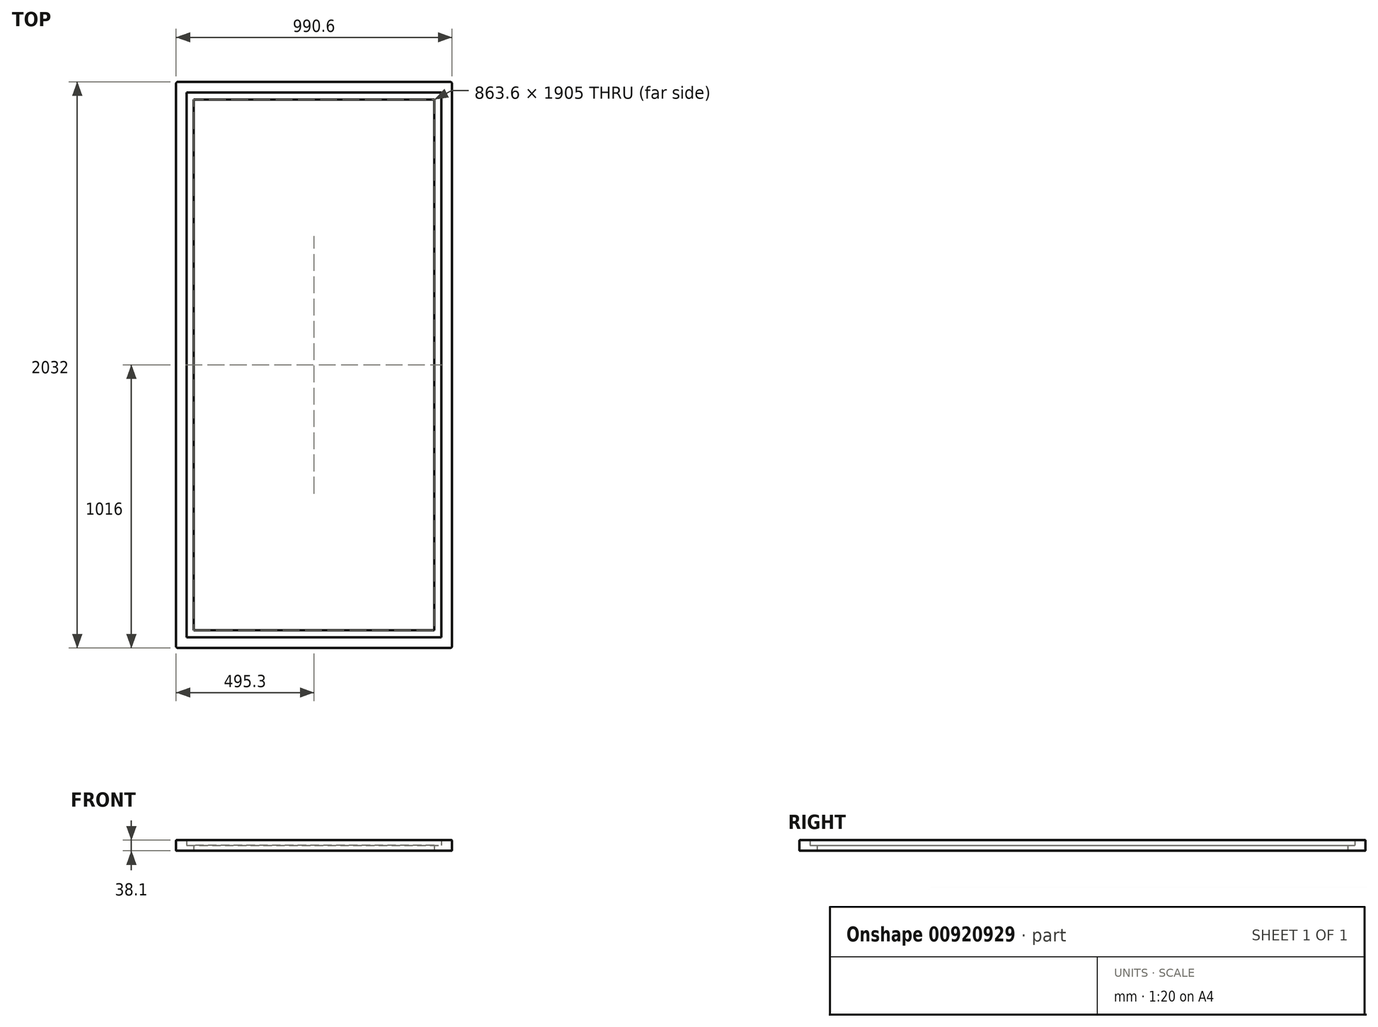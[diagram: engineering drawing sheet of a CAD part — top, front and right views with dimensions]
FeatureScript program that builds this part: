
annotation { "Feature Type Name" : "Feature", "Feature Type Description" : "" }
export const myFeature = defineFeature(function(context is Context, id is Id, definition is map)
    precondition{}
    {
        {
            assignVariable(context, id + "F0", {"name" : "mbrdThick", "anyValue" : 19.05 * mm});
        }
        {
            var Q0;
            Q0=qCreatedBy(makeId("Top.planeOp"),FACE);
            var sketch = newSketch(context, id + "F1", { "sketchPlane" : qUnion([Q0])});
            skLineSegment(sketch, "E0.bottom", {"start": v(-495.3, 1016) * mm, "end": v(495.3, 1016) * mm, "construction": true});
            skLineSegment(sketch, "E0.left", {"start": v(-495.3, 1016) * mm, "end": v(-495.3, -1016) * mm, "construction": true});
            skLineSegment(sketch, "E0.right", {"start": v(495.3, 1016) * mm, "end": v(495.3, -1016) * mm, "construction": true});
            skPoint(sketch, "E0.middle", {"position": v(0, 0) * mm});
            skLineSegment(sketch, "E1.bottom", {"start": v(-495.3, 1016) * mm, "end": v(-431.8, 1016) * mm});
            skLineSegment(sketch, "E1.left", {"start": v(-495.3, 1016) * mm, "end": v(-495.3, -1016) * mm});
            skPoint(sketch, "E2", {"position": v(-431.8, 952.5) * mm});
            skLineSegment(sketch, "E3", {"start": v(-431.8, 952.5) * mm, "end": v(-495.3, 1016) * mm});
            skPoint(sketch, "E4", {"position": v(-431.8, -952.5) * mm});
            skLineSegment(sketch, "E5", {"start": v(-495.3, -1016) * mm, "end": v(-431.8, -952.5) * mm});
            skLineSegment(sketch, "E6", {"start": v(-431.8, 952.5) * mm, "end": v(-431.8, -952.5) * mm});
            skPoint(sketch, "E7", {"position": v(431.8, -952.5) * mm});
            skLineSegment(sketch, "E8", {"start": v(495.3, -1016) * mm, "end": v(431.8, -952.5) * mm});
            skLineSegment(sketch, "E9", {"start": v(431.8, -952.5) * mm, "end": v(-431.8, -952.5) * mm});
            skLineSegment(sketch, "E10", {"start": v(-495.3, -1016) * mm, "end": v(495.3, -1016) * mm});
            skLineSegment(sketch, "E11.1.0", {"start": v(431.8, -952.5) * mm, "end": v(431.8, 952.5) * mm});
            skLineSegment(sketch, "E11.1.1", {"start": v(495.3, -1016) * mm, "end": v(-495.3, -1016) * mm, "construction": true});
            skLineSegment(sketch, "E11.1.3", {"start": v(495.3, -1016) * mm, "end": v(495.3, 1016) * mm, "construction": true});
            skLineSegment(sketch, "E11.1.4", {"start": v(-495.3, -1016) * mm, "end": v(-495.3, 1016) * mm, "construction": true});
            skPoint(sketch, "E11.1.5", {"position": v(431.8, 952.5) * mm});
            skLineSegment(sketch, "E11.1.8", {"start": v(-431.8, 952.5) * mm, "end": v(431.8, 952.5) * mm});
            skLineSegment(sketch, "E11.1.9", {"start": v(495.3, 1016) * mm, "end": v(-495.3, 1016) * mm});
            skLineSegment(sketch, "E11.1.10", {"start": v(495.3, -1016) * mm, "end": v(495.3, 1016) * mm});
            skLineSegment(sketch, "E11.1.11", {"start": v(431.8, -952.5) * mm, "end": v(495.3, -1016) * mm});
            skLineSegment(sketch, "E11.1.12", {"start": v(-495.3, 1016) * mm, "end": v(-431.8, 952.5) * mm});
            skLineSegment(sketch, "E11.1.13", {"start": v(495.3, -1016) * mm, "end": v(431.8, -1016) * mm});
            skLineSegment(sketch, "E11.1.14", {"start": v(495.3, 1016) * mm, "end": v(431.8, 952.5) * mm});
            skLineSegment(sketch, "E11.anchor1", {"start": v(0, 0) * mm, "end": v(-495.3, -1016) * mm, "construction": true});
            skLineSegment(sketch, "E11.anchor2", {"start": v(0, 0) * mm, "end": v(495.3, 1016) * mm, "construction": true});
            skSolve(sketch);
        }
        {
            var Q0;
            Q0=makeQuery(id+"F1.imprint","IMPRINT",FACE,{"disambiguationData":[TD([[makeQuery(id+"F1.imprint","IMPRINT",EDGE,{"derivedFrom":sQuery(id+"F1.wireOp",EDGE,"E11.1.0")}),-1.0]])]});
            var Q1;
            Q1=makeQuery(id+"F1.imprint","IMPRINT",FACE,{"disambiguationData":[TD([[makeQuery(id+"F1.imprint","IMPRINT",EDGE,{"derivedFrom":sQuery(id+"F1.wireOp",EDGE,"E11.1.8")}),1.0]])]});
            var Q2;
            Q2=makeQuery(id+"F1.imprint","IMPRINT",FACE,{"disambiguationData":[TD([[makeQuery(id+"F1.imprint","IMPRINT",EDGE,{"derivedFrom":sQuery(id+"F1.wireOp",EDGE,"E1.left")}),1.0]])]});
            var Q3;
            Q3=makeQuery(id+"F1.imprint","IMPRINT",FACE,{"disambiguationData":[TD([[makeQuery(id+"F1.imprint","IMPRINT",EDGE,{"derivedFrom":sQuery(id+"F1.wireOp",EDGE,"E5")}),-1.0]])]});
            extrude(context, id + "F2", {"entities" : qUnion([Q0, Q1, Q2, Q3]), "depth" : getVariable(context, 'mbrdThick'), "offsetDistance" : 25 * mm});
        }
        {
            var Q0;
            Q0=makeQuery(id+"F2.opExtrude","CAP_FACE",FACE,{"disambiguationData":[OSD([sQuery(id+"F1.wireOp",EDGE,"E1.left"),sQuery(id+"F1.wireOp",EDGE,"E6"),sQuery(id+"F1.wireOp",EDGE,"E9"),sQuery(id+"F1.wireOp",EDGE,"E10"),sQuery(id+"F1.wireOp",EDGE,"E11.1.0"),sQuery(id+"F1.wireOp",EDGE,"E11.1.8"),sQuery(id+"F1.wireOp",EDGE,"E11.1.9"),sQuery(id+"F1.wireOp",EDGE,"E11.1.10"),sQuery(id+"F1.wireOp",EDGE,"E11.1.13")])],"isStart":false});
            var sketch = newSketch(context, id + "F3", { "sketchPlane" : qUnion([Q0])});
            skPoint(sketch, "E12", {"position": v(-457.2, 977.9) * mm});
            skPoint(sketch, "E13", {"position": v(-457.2, -977.9) * mm});
            skPoint(sketch, "E14", {"position": v(457.2, -977.9) * mm});
            skLineSegment(sketch, "E15", {"start": v(-457.2, -977.9) * mm, "end": v(-495.3, -1016) * mm});
            skLineSegment(sketch, "E16", {"start": v(-495.3, -1016) * mm, "end": v(495.3, -1016) * mm});
            skLineSegment(sketch, "E17", {"start": v(495.3, -1016) * mm, "end": v(457.2, -977.9) * mm});
            skLineSegment(sketch, "E18", {"start": v(-457.2, -977.9) * mm, "end": v(457.2, -977.9) * mm});
            skLineSegment(sketch, "E19", {"start": v(-457.2, 977.9) * mm, "end": v(-457.2, -977.9) * mm});
            skLineSegment(sketch, "E20", {"start": v(-495.3, -1016) * mm, "end": v(-495.3, 1016) * mm});
            skLineSegment(sketch, "E21", {"start": v(-495.3, 1016) * mm, "end": v(-457.2, 977.9) * mm});
            skPoint(sketch, "E22.1.0", {"position": v(457.2, 977.9) * mm});
            skLineSegment(sketch, "E22.1.1", {"start": v(495.3, 1016) * mm, "end": v(495.3, -1016) * mm});
            skLineSegment(sketch, "E22.1.2", {"start": v(495.3, 1016) * mm, "end": v(-495.3, 1016) * mm});
            skLineSegment(sketch, "E22.1.5", {"start": v(457.2, -977.9) * mm, "end": v(457.2, 977.9) * mm});
            skLineSegment(sketch, "E22.1.6", {"start": v(457.2, 977.9) * mm, "end": v(-457.2, 977.9) * mm});
            skLineSegment(sketch, "E22.1.8", {"start": v(457.2, 977.9) * mm, "end": v(495.3, 1016) * mm});
            skPoint(sketch, "E22.center", {"position": v(0, 0) * mm});
            skLineSegment(sketch, "E22.anchor1", {"start": v(0, 0) * mm, "end": v(-495.3, -1016) * mm, "construction": true});
            skLineSegment(sketch, "E22.anchor2", {"start": v(0, 0) * mm, "end": v(495.3, 1016) * mm, "construction": true});
            skSolve(sketch);
        }
        {
            var Q0;
            Q0 = qSketchRegion(id + "F3", true);
            extrude(context, id + "F4", {"entities" : qUnion([Q0]), "operationType" : NewBodyOperationType.ADD, "depth" : getVariable(context, 'mbrdThick'), "offsetDistance" : 25 * mm});
        }
        {
            var Q0;
            Q0=makeQuery(id+"F2.opExtrude","CAP_EDGE",EDGE,{"disambiguationData":[OSD([sQuery(id+"F1.wireOp",EDGE,"E1.left")])],"isStart":true});
            var Q1;
            Q1=makeQuery(id+"F4.opExtrude","CAP_EDGE",EDGE,{"disambiguationData":[OSD([sQuery(id+"F3.wireOp",EDGE,"E20")])],"isStart":false});
            var Q2;
            Q2=makeQuery(id+"F4.opExtrude","CAP_EDGE",EDGE,{"disambiguationData":[OSD([sQuery(id+"F3.wireOp",EDGE,"E16")])],"isStart":false});
            var Q3;
            Q3=makeQuery(id+"F2.opExtrude","CAP_EDGE",EDGE,{"disambiguationData":[OSD([sQuery(id+"F1.wireOp",EDGE,"E10"),sQuery(id+"F1.wireOp",EDGE,"E11.1.13")])],"isStart":true});
            var Q4;
            Q4=makeQuery(id+"F4.opExtrude","CAP_EDGE",EDGE,{"disambiguationData":[OSD([sQuery(id+"F3.wireOp",EDGE,"E22.1.1")])],"isStart":false});
            var Q5;
            Q5=makeQuery(id+"F2.opExtrude","CAP_EDGE",EDGE,{"disambiguationData":[OSD([sQuery(id+"F1.wireOp",EDGE,"E11.1.10")])],"isStart":true});
            var Q6;
            Q6=makeQuery(id+"F4.opExtrude","CAP_EDGE",EDGE,{"disambiguationData":[OSD([sQuery(id+"F3.wireOp",EDGE,"E22.1.2")])],"isStart":false});
            var Q7;
            Q7=makeQuery(id+"F2.opExtrude","CAP_EDGE",EDGE,{"disambiguationData":[OSD([sQuery(id+"F1.wireOp",EDGE,"E11.1.9")])],"isStart":true});
            fillet(context, id + "F5", {"entities" : qUnion([Q0, Q1, Q2, Q3, Q4, Q5, Q6, Q7]), "radius" : 1.59 * mm, "tangentPropagation" : true, "allowEdgeOverflow" : false});
        }
        {
            var Q0;
            Q0=makeQuery(id+"F4.boolean.opBoolean","MERGE",EDGE,{"derivedFrom":[makeQuery(id+"F2.opExtrude","SWEPT_EDGE",EDGE,{"disambiguationData":[OSD([sQuery(id+"F1.wireOp",EDGE,"E1.left"),sQuery(id+"F1.wireOp",EDGE,"E11.1.9"),sQuery(id+"F1.wireOp",EDGE,"E11.1.12")])]}),makeQuery(id+"F4.opExtrude","SWEPT_EDGE",EDGE,{"disambiguationData":[OSD([sQuery(id+"F3.wireOp",EDGE,"E20"),sQuery(id+"F3.wireOp",EDGE,"E22.1.2"),sQuery(id+"F3.wireOp",EDGE,"E21")])]})]});
            var Q1;
            Q1=makeQuery(id+"F4.boolean.opBoolean","MERGE",EDGE,{"derivedFrom":[makeQuery(id+"F2.opExtrude","SWEPT_EDGE",EDGE,{"disambiguationData":[OSD([sQuery(id+"F1.wireOp",EDGE,"E1.left"),sQuery(id+"F1.wireOp",EDGE,"E5"),sQuery(id+"F1.wireOp",EDGE,"E10")])]}),makeQuery(id+"F4.opExtrude","SWEPT_EDGE",EDGE,{"disambiguationData":[OSD([sQuery(id+"F3.wireOp",EDGE,"E15"),sQuery(id+"F3.wireOp",EDGE,"E16"),sQuery(id+"F3.wireOp",EDGE,"E20")])]})]});
            var Q2;
            Q2=makeQuery(id+"F4.boolean.opBoolean","MERGE",EDGE,{"derivedFrom":[makeQuery(id+"F2.opExtrude","SWEPT_EDGE",EDGE,{"disambiguationData":[OSD([sQuery(id+"F1.wireOp",EDGE,"E11.1.10"),sQuery(id+"F1.wireOp",EDGE,"E11.1.11"),sQuery(id+"F1.wireOp",EDGE,"E11.1.13")])]}),makeQuery(id+"F4.opExtrude","SWEPT_EDGE",EDGE,{"disambiguationData":[OSD([sQuery(id+"F3.wireOp",EDGE,"E16"),sQuery(id+"F3.wireOp",EDGE,"E22.1.1"),sQuery(id+"F3.wireOp",EDGE,"E17")])]})]});
            var Q3;
            Q3=makeQuery(id+"F4.boolean.opBoolean","MERGE",EDGE,{"derivedFrom":[makeQuery(id+"F2.opExtrude","SWEPT_EDGE",EDGE,{"disambiguationData":[OSD([sQuery(id+"F1.wireOp",EDGE,"E11.1.9"),sQuery(id+"F1.wireOp",EDGE,"E11.1.10"),sQuery(id+"F1.wireOp",EDGE,"E11.1.14")])]}),makeQuery(id+"F4.opExtrude","SWEPT_EDGE",EDGE,{"disambiguationData":[OSD([sQuery(id+"F3.wireOp",EDGE,"E22.1.1"),sQuery(id+"F3.wireOp",EDGE,"E22.1.2"),sQuery(id+"F3.wireOp",EDGE,"E22.1.8")])]})]});
            fillet(context, id + "F6", {"entities" : qUnion([Q0, Q1, Q2, Q3]), "radius" : 6.35 * mm, "tangentPropagation" : true, "allowEdgeOverflow" : false});
        }
    });
